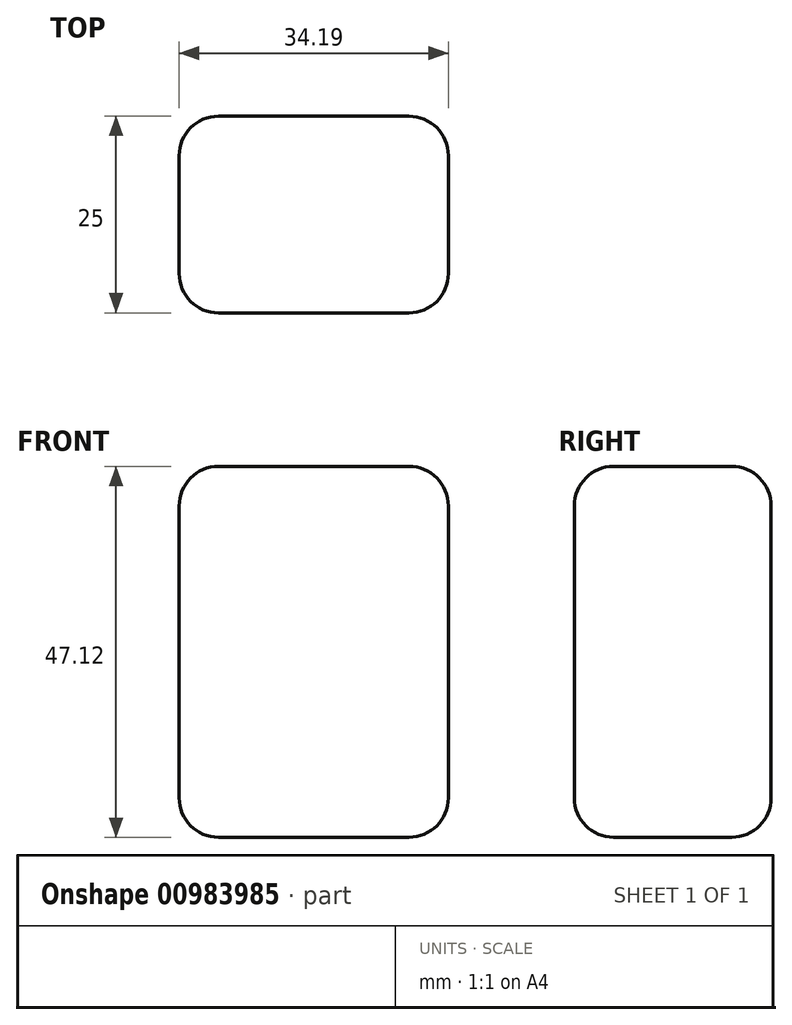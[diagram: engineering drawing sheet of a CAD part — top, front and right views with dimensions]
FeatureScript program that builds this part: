
annotation { "Feature Type Name" : "Feature", "Feature Type Description" : "" }
export const myFeature = defineFeature(function(context is Context, id is Id, definition is map)
    precondition{}
    {
        {
            var Q0;
            Q0=qCreatedBy(makeId("Front.planeOp"),FACE);
            var sketch = newSketch(context, id + "F0", { "sketchPlane" : qUnion([Q0])});
            skLineSegment(sketch, "E0.bottom", {"start": v(-112.07, 57.51) * mm, "end": v(-77.88, 57.51) * mm});
            skLineSegment(sketch, "E0.top", {"start": v(-112.07, 10.4) * mm, "end": v(-77.88, 10.4) * mm});
            skLineSegment(sketch, "E0.left", {"start": v(-112.07, 57.51) * mm, "end": v(-112.07, 10.4) * mm});
            skLineSegment(sketch, "E0.right", {"start": v(-77.88, 57.51) * mm, "end": v(-77.88, 10.4) * mm});
            skSolve(sketch);
        }
        {
            var Q0;
            Q0 = qSketchRegion(id + "F0", true);
            extrude(context, id + "F1", {"entities" : qUnion([Q0]), "depth" : 25 * mm, "offsetDistance" : 25 * mm});
        }
        {
            var Q0;
            Q0=makeQuery(id+"F1.opExtrude","SWEPT_EDGE",EDGE,{"disambiguationData":[OSD([sQuery(id+"F0.wireOp",EDGE,"E0.bottom"),sQuery(id+"F0.wireOp",EDGE,"E0.left")])]});
            var Q1;
            Q1=makeQuery(id+"F1.opExtrude","SWEPT_EDGE",EDGE,{"disambiguationData":[OSD([sQuery(id+"F0.wireOp",EDGE,"E0.bottom"),sQuery(id+"F0.wireOp",EDGE,"E0.right")])]});
            var Q2;
            Q2=makeQuery(id+"F1.opExtrude","SWEPT_EDGE",EDGE,{"disambiguationData":[OSD([sQuery(id+"F0.wireOp",EDGE,"E0.top"),sQuery(id+"F0.wireOp",EDGE,"E0.right")])]});
            var Q3;
            Q3=makeQuery(id+"F1.opExtrude","CAP_EDGE",EDGE,{"disambiguationData":[OSD([sQuery(id+"F0.wireOp",EDGE,"E0.bottom")])],"isStart":true});
            var Q4;
            Q4=makeQuery(id+"F1.opExtrude","CAP_EDGE",EDGE,{"disambiguationData":[OSD([sQuery(id+"F0.wireOp",EDGE,"E0.bottom")])],"isStart":false});
            var Q5;
            Q5=makeQuery(id+"F1.opExtrude","CAP_EDGE",EDGE,{"disambiguationData":[OSD([sQuery(id+"F0.wireOp",EDGE,"E0.top")])],"isStart":false});
            var Q6;
            Q6=makeQuery(id+"F1.opExtrude","SWEPT_EDGE",EDGE,{"disambiguationData":[OSD([sQuery(id+"F0.wireOp",EDGE,"E0.top"),sQuery(id+"F0.wireOp",EDGE,"E0.left")])]});
            var Q7;
            Q7=makeQuery(id+"F1.opExtrude","CAP_EDGE",EDGE,{"disambiguationData":[OSD([sQuery(id+"F0.wireOp",EDGE,"E0.top")])],"isStart":true});
            var Q8;
            Q8=makeQuery(id+"F1.opExtrude","CAP_EDGE",EDGE,{"disambiguationData":[OSD([sQuery(id+"F0.wireOp",EDGE,"E0.left")])],"isStart":true});
            var Q9;
            Q9=makeQuery(id+"F1.opExtrude","CAP_EDGE",EDGE,{"disambiguationData":[OSD([sQuery(id+"F0.wireOp",EDGE,"E0.left")])],"isStart":false});
            var Q10;
            Q10=makeQuery(id+"F1.opExtrude","CAP_EDGE",EDGE,{"disambiguationData":[OSD([sQuery(id+"F0.wireOp",EDGE,"E0.right")])],"isStart":true});
            var Q11;
            Q11=makeQuery(id+"F1.opExtrude","CAP_EDGE",EDGE,{"disambiguationData":[OSD([sQuery(id+"F0.wireOp",EDGE,"E0.right")])],"isStart":false});
            fillet(context, id + "F2", {"entities" : qUnion([Q0, Q1, Q2, Q3, Q4, Q5, Q6, Q7, Q8, Q9, Q10, Q11]), "radius" : 5 * mm, "tangentPropagation" : true, "allowEdgeOverflow" : false});
        }
    });
